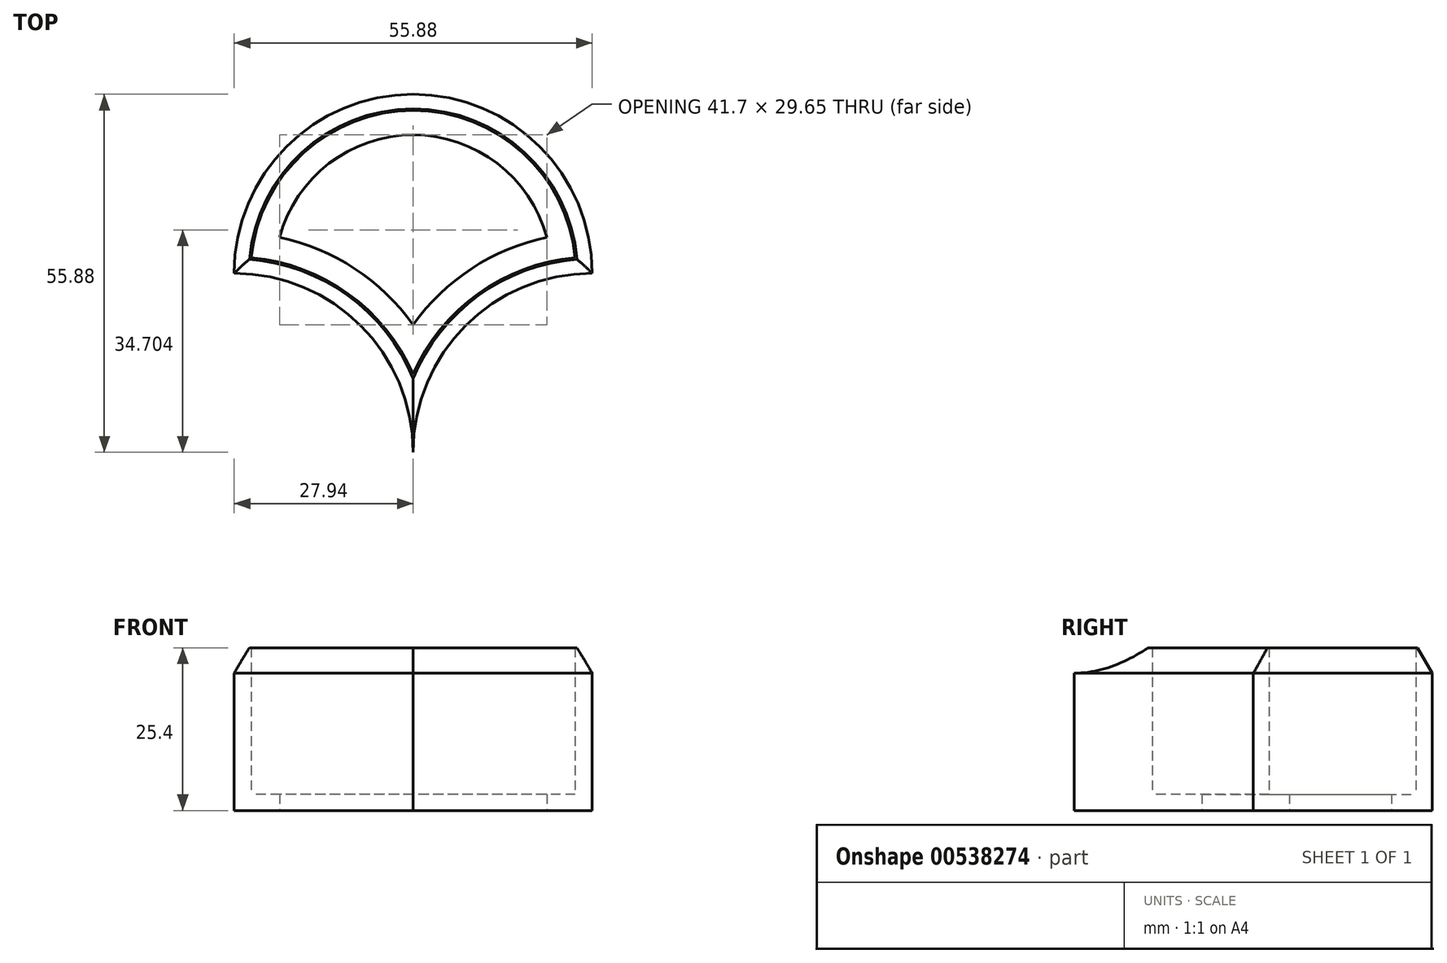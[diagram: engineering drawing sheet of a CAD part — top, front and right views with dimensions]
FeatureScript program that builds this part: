
annotation { "Feature Type Name" : "Feature", "Feature Type Description" : "" }
export const myFeature = defineFeature(function(context is Context, id is Id, definition is map)
    precondition{}
    {
        {
            var Q0;
            Q0=qCreatedBy(makeId("Top.planeOp"),FACE);
            var sketch = newSketch(context, id + "F0", { "sketchPlane" : qUnion([Q0])});
            skCircle(sketch, "E0", {"center": v(0, 0) * mm, "radius": 27.94 * mm});
            skPoint(sketch, "E1", {"position": v(0, -27.94) * mm});
            skPoint(sketch, "E2", {"position": v(-27.94, 0) * mm});
            skCircle(sketch, "E3", {"center": v(-27.94, -27.94) * mm, "radius": 27.94 * mm});
            skPoint(sketch, "E3.third.point", {"position": v(-45.74, -49.48) * mm});
            skLineSegment(sketch, "E4", {"start": v(-27.94, 0) * mm, "end": v(27.94, 0) * mm, "construction": true});
            skCircle(sketch, "E5", {"center": v(27.94, -27.94) * mm, "radius": 27.94 * mm});
            skPoint(sketch, "E5.third.point", {"position": v(40.8, -52.74) * mm});
            skSolve(sketch);
        }
        {
            var Q0;
            {var subQ0=sQuery(id+"F0.wireOp",EDGE,"E3");var subQ1=sQuery(id+"F0.wireOp",EDGE,"E0");var subQ2=makeQuery(id+"F0.imprint","INTERSECT",VERTEX,{"derivedFrom":[subQ1,subQ0]});Q0=makeQuery(id+"F0.imprint","IMPRINT",FACE,{"disambiguationData":[TD([[makeQuery(id+"F0.imprint","IMPRINT",EDGE,{"disambiguationData":[TD([[subQ2,1.0]])],"derivedFrom":subQ1}),1.0]])]});}
            extrude(context, id + "F1", {"entities" : qUnion([Q0]), "depth" : 25.4 * mm, "offsetDistance" : 25.4 * mm});
        }
        {
            var Q0;
            Q0=makeQuery(id+"F1.opExtrude","CAP_FACE",FACE,{"disambiguationData":[OSD([sQuery(id+"F0.wireOp",EDGE,"E0"),sQuery(id+"F0.wireOp",EDGE,"E3"),sQuery(id+"F0.wireOp",EDGE,"E5")])],"isStart":false});
            shell(context, id + "F2", {"entities" : qUnion([Q0]), "thickness" : 2.54 * mm});
        }
        {
            var Q0;
            Q0=makeQuery(id+"F1.opExtrude","CAP_EDGE",EDGE,{"disambiguationData":[OSD([sQuery(id+"F0.wireOp",EDGE,"E0")])],"isStart":false});
            var Q1;
            Q1=makeQuery(id+"F1.opExtrude","CAP_EDGE",EDGE,{"disambiguationData":[OSD([sQuery(id+"F0.wireOp",EDGE,"E3")])],"isStart":false});
            var Q2;
            Q2=makeQuery(id+"F1.opExtrude","CAP_EDGE",EDGE,{"disambiguationData":[OSD([sQuery(id+"F0.wireOp",EDGE,"E5")])],"isStart":false});
            chamfer(context, id + "F3", {"entities" : qUnion([Q0, Q1, Q2]), "chamferType" : ChamferType.OFFSET_ANGLE, "width" : 2.3 * mm, "oppositeDirection" : false, "angle" : 60 * degree, "tangentPropagation" : true});
        }
        {
            var Q0;
            Q0=makeQuery(id+"F1.opExtrude","CAP_FACE",FACE,{"disambiguationData":[OSD([sQuery(id+"F0.wireOp",EDGE,"E0"),sQuery(id+"F0.wireOp",EDGE,"E3"),sQuery(id+"F0.wireOp",EDGE,"E5")])],"isStart":true});
            var sketch = newSketch(context, id + "F4", { "sketchPlane" : qUnion([Q0])});
            skArc(sketch, "E6.0", {"start": v(20.85, -5.6) * mm, "mid": v(0, -21.59) * mm, "end": v(-20.85, -5.6) * mm});
            skArc(sketch, "E6.1", {"start": v(20.85, -5.6) * mm, "mid": v(9.14, -0.74) * mm, "end": v(0, 8.06) * mm});
            skArc(sketch, "E6.2", {"start": v(0, 8.06) * mm, "mid": v(-9.14, -0.74) * mm, "end": v(-20.85, -5.6) * mm});
            skSolve(sketch);
        }
        {
            var Q0;
            Q0 = qSketchRegion(id + "F4", true);
            var Q1;
            Q1=makeQuery(id+"F1.opExtrude","SWEPT_BODY",BODY,{"disambiguationData":[OSD([sQuery(id+"F0.wireOp",EDGE,"E0"),sQuery(id+"F0.wireOp",EDGE,"E3"),sQuery(id+"F0.wireOp",EDGE,"E5")])]});
            extrude(context, id + "F5", {"entities" : qUnion([Q0]), "operationType" : NewBodyOperationType.REMOVE, "endBound" : BoundingType.UP_TO_BODY, "oppositeDirection" : true, "depth" : 25.4 * mm, "endBoundEntityBody" : qUnion([Q1]), "offsetDistance" : 25.4 * mm});
        }
    });
